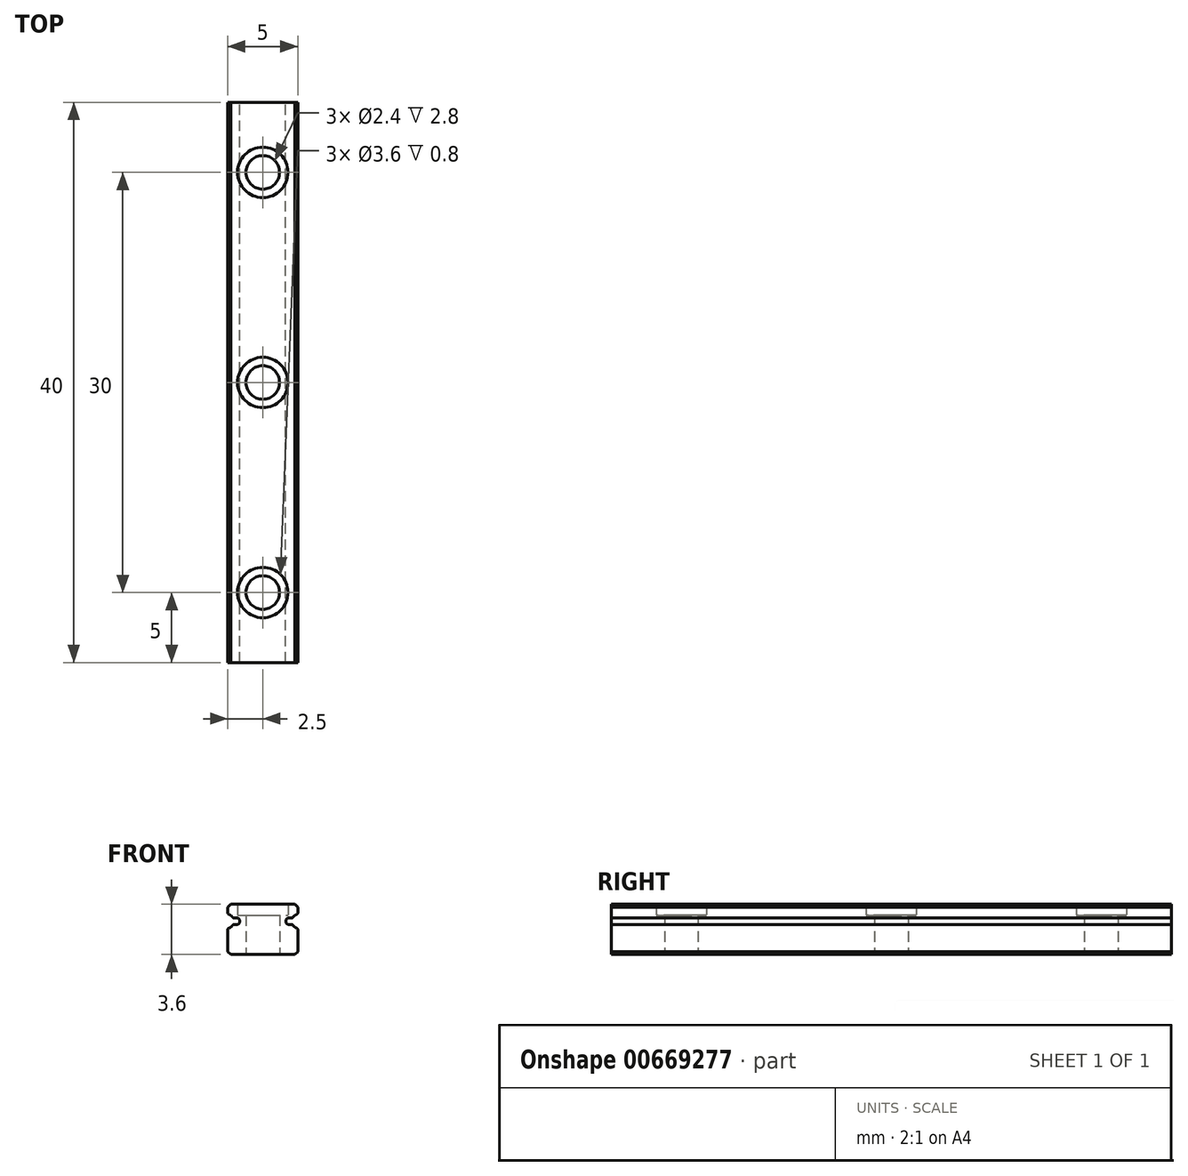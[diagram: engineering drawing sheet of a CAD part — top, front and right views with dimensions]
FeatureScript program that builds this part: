
annotation { "Feature Type Name" : "Feature", "Feature Type Description" : "" }
export const myFeature = defineFeature(function(context is Context, id is Id, definition is map)
    precondition{}
    {
        {
            var Q0;
            Q0=qCreatedBy(makeId("Front.planeOp"),FACE);
            var sketch = newSketch(context, id + "F0", { "sketchPlane" : qUnion([Q0]), "disableImprinting" : false});
            skLineSegment(sketch, "E0.bottom", {"start": v(2.29, -1.8) * mm, "end": v(-2.29, -1.8) * mm});
            skLineSegment(sketch, "E0.top", {"start": v(2.29, 1.8) * mm, "end": v(-2.29, 1.8) * mm});
            skLineSegment(sketch, "E0.left", {"start": v(2.5, -1.59) * mm, "end": v(2.5, -0.03) * mm});
            skLineSegment(sketch, "E0.right", {"start": v(-2.5, -1.59) * mm, "end": v(-2.5, -0.03) * mm});
            skPoint(sketch, "E0.middle", {"position": v(0, 0) * mm});
            skArc(sketch, "E1", {"start": v(-2.42, 0.09) * mm, "mid": v(-2.28, 0.17) * mm, "end": v(-2.17, 0.29) * mm});
            skArc(sketch, "E2", {"start": v(2.42, 1.06) * mm, "mid": v(2.28, 0.98) * mm, "end": v(2.17, 0.86) * mm});
            skArc(sketch, "E3", {"start": v(-1.88, 0.34) * mm, "mid": v(-1.64, 0.57) * mm, "end": v(-1.87, 0.8) * mm});
            skArc(sketch, "E4", {"start": v(1.87, 0.8) * mm, "mid": v(1.64, 0.57) * mm, "end": v(1.88, 0.34) * mm});
            skLineSegment(sketch, "E5", {"start": v(1.87, 0.8) * mm, "end": v(2.07, 0.8) * mm});
            skLineSegment(sketch, "E6", {"start": v(1.88, 0.34) * mm, "end": v(2.07, 0.34) * mm});
            skLineSegment(sketch, "E7", {"start": v(-1.88, 0.34) * mm, "end": v(-2.07, 0.34) * mm});
            skLineSegment(sketch, "E8", {"start": v(-1.87, 0.8) * mm, "end": v(-2.07, 0.8) * mm});
            skLineSegment(sketch, "E9", {"start": v(-2.5, 1.59) * mm, "end": v(-2.29, 1.8) * mm});
            skLineSegment(sketch, "E10.MirrorCS", {"start": v(2.5, 1.59) * mm, "end": v(2.29, 1.8) * mm});
            skLineSegment(sketch, "E11.MirrorCS", {"start": v(2.5, -1.59) * mm, "end": v(2.29, -1.8) * mm});
            skLineSegment(sketch, "E12.MirrorCS", {"start": v(-2.5, -1.59) * mm, "end": v(-2.29, -1.8) * mm});
            skPoint(sketch, "E13.orphan", {"position": v(-2.5, 1.8) * mm});
            skLineSegment(sketch, "E14.trimOffspring", {"start": v(-2.5, 1.18) * mm, "end": v(-2.5, 1.59) * mm});
            skArc(sketch, "E15.trimOffspring", {"start": v(-2.17, 0.86) * mm, "mid": v(-2.28, 0.98) * mm, "end": v(-2.42, 1.06) * mm});
            skPoint(sketch, "E16.orphan", {"position": v(2.5, 1.8) * mm});
            skLineSegment(sketch, "E17.trimOffspring", {"start": v(2.5, 1.18) * mm, "end": v(2.5, 1.59) * mm});
            skArc(sketch, "E18.trimOffspring", {"start": v(2.17, 0.29) * mm, "mid": v(2.28, 0.17) * mm, "end": v(2.42, 0.09) * mm});
            skPoint(sketch, "E19.orphan", {"position": v(2.5, -1.8) * mm});
            skPoint(sketch, "E20.orphan", {"position": v(-2.5, -1.8) * mm});
            skPoint(sketch, "E21.0.visualSharp", {"position": v(2.5, 1.09) * mm});
            skArc(sketch, "E21.0.filletArc", {"start": v(2.42, 1.06) * mm, "mid": v(2.48, 1.1) * mm, "end": v(2.5, 1.18) * mm});
            skPoint(sketch, "E21.1.visualSharp", {"position": v(2.5, 0.06) * mm});
            skArc(sketch, "E21.1.filletArc", {"start": v(2.5, -0.03) * mm, "mid": v(2.48, 0.04) * mm, "end": v(2.42, 0.09) * mm});
            skPoint(sketch, "E21.2.visualSharp", {"position": v(-2.5, 0.06) * mm});
            skArc(sketch, "E21.2.filletArc", {"start": v(-2.42, 0.09) * mm, "mid": v(-2.48, 0.04) * mm, "end": v(-2.5, -0.03) * mm});
            skPoint(sketch, "E21.3.visualSharp", {"position": v(-2.5, 1.09) * mm});
            skArc(sketch, "E21.3.filletArc", {"start": v(-2.5, 1.18) * mm, "mid": v(-2.48, 1.1) * mm, "end": v(-2.42, 1.06) * mm});
            skPoint(sketch, "E22.0.visualSharp", {"position": v(2.14, 0.8) * mm});
            skArc(sketch, "E22.0.filletArc", {"start": v(2.07, 0.81) * mm, "mid": v(2.12, 0.82) * mm, "end": v(2.17, 0.86) * mm});
            skPoint(sketch, "E22.1.visualSharp", {"position": v(2.14, 0.34) * mm});
            skArc(sketch, "E22.1.filletArc", {"start": v(2.17, 0.29) * mm, "mid": v(2.12, 0.33) * mm, "end": v(2.07, 0.34) * mm});
            skPoint(sketch, "E22.2.visualSharp", {"position": v(-2.14, 0.34) * mm});
            skArc(sketch, "E22.2.filletArc", {"start": v(-2.07, 0.34) * mm, "mid": v(-2.12, 0.33) * mm, "end": v(-2.17, 0.29) * mm});
            skPoint(sketch, "E22.3.visualSharp", {"position": v(-2.14, 0.8) * mm});
            skArc(sketch, "E22.3.filletArc", {"start": v(-2.17, 0.86) * mm, "mid": v(-2.12, 0.82) * mm, "end": v(-2.07, 0.81) * mm});
            skSolve(sketch);
        }
        {
            var Q0;
            Q0=makeQuery(id+"F0.imprint","IMPRINT",FACE,{"disambiguationData":[TD([[makeQuery(id+"F0.imprint","IMPRINT",EDGE,{"derivedFrom":sQuery(id+"F0.wireOp",EDGE,"E0.bottom")}),-1.0]])]});
            extrude(context, id + "F1", {"entities" : qUnion([Q0]), "depth" : 40 * mm, "offsetDistance" : 25 * mm});
        }
        {
            var Q0;
            Q0=makeQuery(id+"F1.opExtrude","SWEPT_FACE",FACE,{"disambiguationData":[OSD([sQuery(id+"F0.wireOp",EDGE,"E0.top")])]});
            var sketch = newSketch(context, id + "F2", { "sketchPlane" : qUnion([Q0])});
            skPoint(sketch, "E23", {"position": v(0, -5) * mm});
            skPoint(sketch, "E24.1.0.0", {"position": v(0, -20) * mm});
            skPoint(sketch, "E24.2.0.0", {"position": v(0, -35) * mm});
            skPoint(sketch, "E24.3.0.0", {"position": v(0, -50) * mm});
            skPoint(sketch, "E24.4.0.0", {"position": v(0, -65) * mm});
            skPoint(sketch, "E24.5.0.0", {"position": v(0, -80) * mm});
            skPoint(sketch, "E24.6.0.0", {"position": v(0, -95) * mm});
            skPoint(sketch, "E24.7.0.0", {"position": v(0, -110) * mm});
            skPoint(sketch, "E24.8.0.0", {"position": v(0, -125) * mm});
            skPoint(sketch, "E24.9.0.0", {"position": v(0, -140) * mm});
            skPoint(sketch, "E24.10.0.0", {"position": v(0, -155) * mm});
            skPoint(sketch, "E24.11.0.0", {"position": v(0, -170) * mm});
            skPoint(sketch, "E24.12.0.0", {"position": v(0, -185) * mm});
            skPoint(sketch, "E24.13.0.0", {"position": v(0, -200) * mm});
            skPoint(sketch, "E24.14.0.0", {"position": v(0, -215) * mm});
            skPoint(sketch, "E24.15.0.0", {"position": v(0, -230) * mm});
            skPoint(sketch, "E24.16.0.0", {"position": v(0, -245) * mm});
            skLineSegment(sketch, "E24.direction1", {"start": v(0, -5) * mm, "end": v(0, -20) * mm, "construction": true});
            skSolve(sketch);
        }
        {
            var Q0;
            Q0=sQuery(id+"F2.wireOp",VERTEX,"E24.5.0.0");
            var Q1;
            Q1=sQuery(id+"F2.wireOp",VERTEX,"E24.6.0.0");
            var Q2;
            Q2=sQuery(id+"F2.wireOp",VERTEX,"E24.7.0.0");
            var Q3;
            Q3=sQuery(id+"F2.wireOp",VERTEX,"E24.8.0.0");
            var Q4;
            Q4=sQuery(id+"F2.wireOp",VERTEX,"E24.9.0.0");
            var Q5;
            Q5=sQuery(id+"F2.wireOp",VERTEX,"E24.10.0.0");
            var Q6;
            Q6=sQuery(id+"F2.wireOp",VERTEX,"E24.11.0.0");
            var Q7;
            Q7=sQuery(id+"F2.wireOp",VERTEX,"E24.15.0.0");
            var Q8;
            Q8=sQuery(id+"F2.wireOp",VERTEX,"E24.14.0.0");
            var Q9;
            Q9=sQuery(id+"F2.wireOp",VERTEX,"E24.12.0.0");
            var Q10;
            Q10=sQuery(id+"F2.wireOp",VERTEX,"E24.13.0.0");
            var Q11;
            Q11=sQuery(id+"F2.wireOp",VERTEX,"E23");
            var Q12;
            Q12=sQuery(id+"F2.wireOp",VERTEX,"E24.1.0.0");
            var Q13;
            Q13=sQuery(id+"F2.wireOp",VERTEX,"E24.2.0.0");
            var Q14;
            Q14=sQuery(id+"F2.wireOp",VERTEX,"E24.3.0.0");
            var Q15;
            Q15=sQuery(id+"F2.wireOp",VERTEX,"E24.4.0.0");
            var Q16;
            Q16=sQuery(id+"F2.wireOp",VERTEX,"E24.16.0.0");
            var Q17;
            Q17=makeQuery(id+"F1.opExtrude","SWEPT_BODY",BODY,{"disambiguationData":[OSD([sQuery(id+"F0.wireOp",EDGE,"E0.bottom"),sQuery(id+"F0.wireOp",EDGE,"E0.top"),sQuery(id+"F0.wireOp",EDGE,"E0.left"),sQuery(id+"F0.wireOp",EDGE,"E0.right"),sQuery(id+"F0.wireOp",EDGE,"E1"),sQuery(id+"F0.wireOp",EDGE,"E2"),sQuery(id+"F0.wireOp",EDGE,"E3"),sQuery(id+"F0.wireOp",EDGE,"E4"),sQuery(id+"F0.wireOp",EDGE,"E5"),sQuery(id+"F0.wireOp",EDGE,"E6"),sQuery(id+"F0.wireOp",EDGE,"E7"),sQuery(id+"F0.wireOp",EDGE,"E8"),sQuery(id+"F0.wireOp",EDGE,"E9"),sQuery(id+"F0.wireOp",EDGE,"E10.MirrorCS"),sQuery(id+"F0.wireOp",EDGE,"E11.MirrorCS"),sQuery(id+"F0.wireOp",EDGE,"E12.MirrorCS"),sQuery(id+"F0.wireOp",EDGE,"E14.trimOffspring"),sQuery(id+"F0.wireOp",EDGE,"E15.trimOffspring"),sQuery(id+"F0.wireOp",EDGE,"E17.trimOffspring"),sQuery(id+"F0.wireOp",EDGE,"E18.trimOffspring")])]});
            hole(context, id + "F3", {"style" : HoleStyle.C_BORE, "endStyle" : HoleEndStyle.THROUGH, "holeDiameter" : 2.4 * mm, "cBoreDiameter" : 3.6 * mm, "cBoreDepth" : 0.8 * mm, "majorDiameter" : 5 * mm, "isTappedThrough" : true, "tappedDepth" : 12 * mm, "tapClearance" : 3, "locations" : qUnion([Q0, Q1, Q2, Q3, Q4, Q5, Q6, Q7, Q8, Q9, Q10, Q11, Q12, Q13, Q14, Q15, Q16]), "scope" : qUnion([Q17]), "startStyle" : HoleStartStyle.PART});
        }
    });
